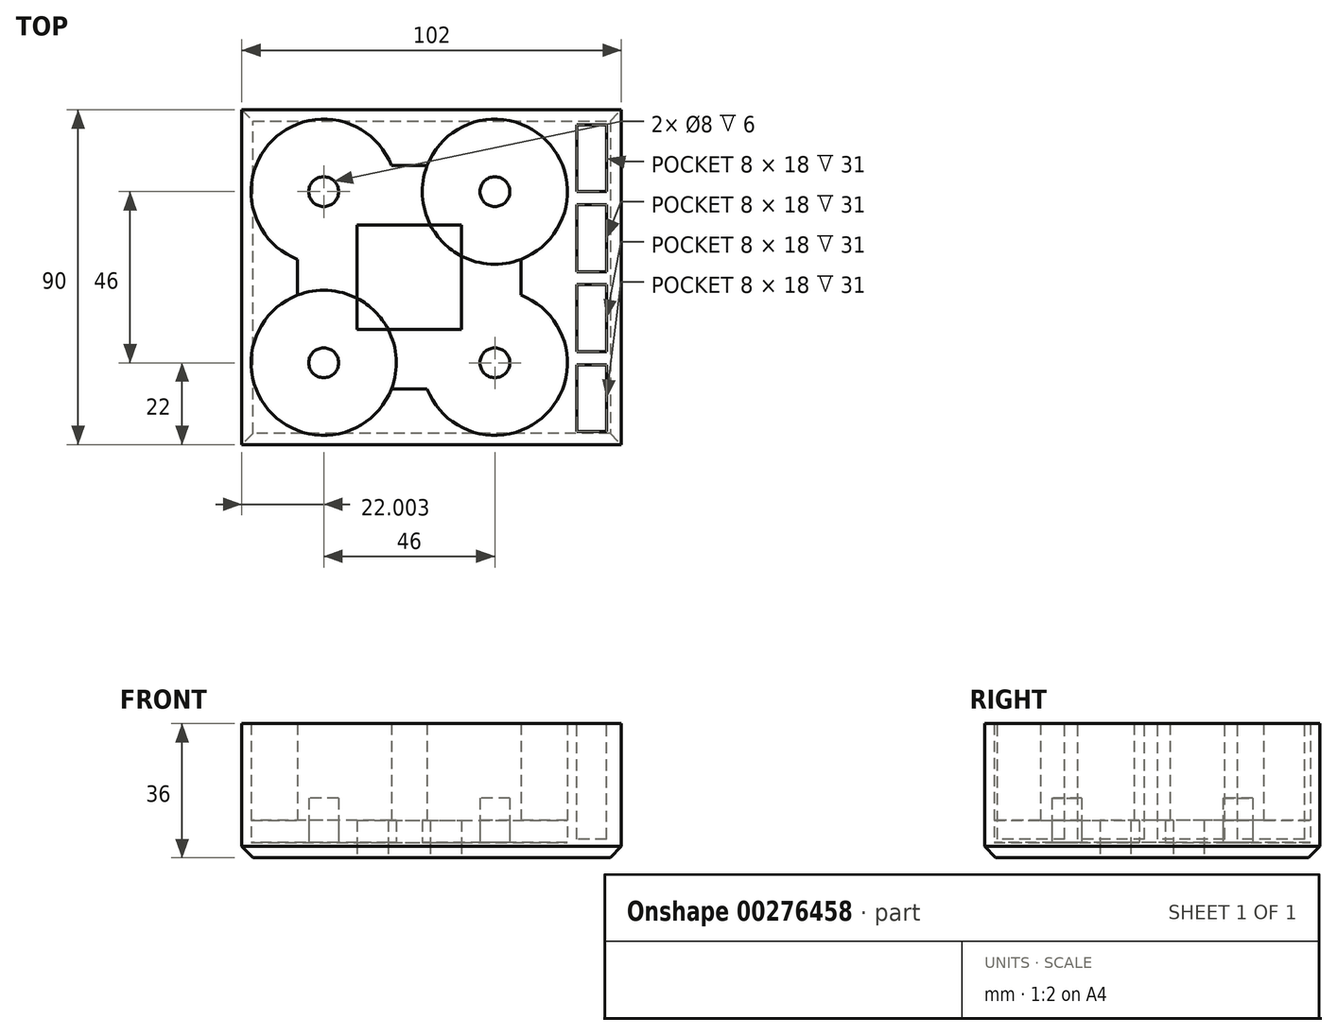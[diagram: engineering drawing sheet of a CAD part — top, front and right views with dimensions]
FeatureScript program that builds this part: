
annotation { "Feature Type Name" : "Feature", "Feature Type Description" : "" }
export const myFeature = defineFeature(function(context is Context, id is Id, definition is map)
    precondition{}
    {
        {
            var Q0;
            Q0=qCreatedBy(makeId("Top.planeOp"),FACE);
            var sketch = newSketch(context, id + "F0", { "sketchPlane" : qUnion([Q0])});
            skLineSegment(sketch, "E0.bottom", {"start": v(-22.74, 29.48) * mm, "end": v(31.26, 29.48) * mm, "construction": true});
            skLineSegment(sketch, "E0.top", {"start": v(-22.74, -24.52) * mm, "end": v(31.26, -24.52) * mm, "construction": true});
            skLineSegment(sketch, "E0.left", {"start": v(-22.74, 29.48) * mm, "end": v(-22.74, -24.52) * mm, "construction": true});
            skLineSegment(sketch, "E0.right", {"start": v(31.26, 29.48) * mm, "end": v(31.26, -24.52) * mm, "construction": true});
            skCircle(sketch, "E1", {"center": v(-18.74, 25.48) * mm, "radius": 4 * mm});
            skLineSegment(sketch, "E2", {"start": v(4.26, 29.48) * mm, "end": v(4.26, -24.52) * mm, "construction": true});
            skLineSegment(sketch, "E3", {"start": v(-22.74, 2.48) * mm, "end": v(31.26, 2.48) * mm, "construction": true});
            skCircle(sketch, "E4.MirrorC", {"center": v(27.26, 25.48) * mm, "radius": 4 * mm});
            skCircle(sketch, "E5.MirrorC", {"center": v(-18.74, -20.52) * mm, "radius": 4 * mm});
            skCircle(sketch, "E6.MirrorC", {"center": v(27.26, -20.52) * mm, "radius": 4 * mm});
            skCircle(sketch, "E7", {"center": v(-18.74, 25.48) * mm, "radius": 19.5 * mm});
            skCircle(sketch, "E8.MirrorC", {"center": v(27.26, 25.48) * mm, "radius": 19.5 * mm});
            skCircle(sketch, "E9.MirrorC", {"center": v(-18.74, -20.52) * mm, "radius": 19.5 * mm});
            skCircle(sketch, "E10.MirrorC", {"center": v(27.26, -20.52) * mm, "radius": 19.5 * mm});
            skLineSegment(sketch, "E11.bottom", {"start": v(-9.74, 16.48) * mm, "end": v(18.26, 16.48) * mm});
            skLineSegment(sketch, "E11.top", {"start": v(-9.74, -11.52) * mm, "end": v(18.26, -11.52) * mm});
            skLineSegment(sketch, "E11.left", {"start": v(-9.74, 16.48) * mm, "end": v(-9.74, -11.52) * mm});
            skLineSegment(sketch, "E11.right", {"start": v(18.26, 16.48) * mm, "end": v(18.26, -11.52) * mm});
            skLineSegment(sketch, "E12", {"start": v(-0.54, 32.48) * mm, "end": v(9.06, 32.48) * mm});
            skLineSegment(sketch, "E13.MirrorCS", {"start": v(-0.54, -27.52) * mm, "end": v(9.06, -27.52) * mm});
            skLineSegment(sketch, "E14", {"start": v(34.26, 7.28) * mm, "end": v(34.26, -2.32) * mm});
            skLineSegment(sketch, "E15.MirrorCS", {"start": v(-25.74, 7.28) * mm, "end": v(-25.74, -2.32) * mm});
            skLineSegment(sketch, "E16.bottom", {"start": v(-40.74, 47.48) * mm, "end": v(49.26, 47.48) * mm});
            skLineSegment(sketch, "E16.top", {"start": v(-40.74, -42.52) * mm, "end": v(49.26, -42.52) * mm});
            skLineSegment(sketch, "E16.left", {"start": v(-40.74, 47.48) * mm, "end": v(-40.74, -42.52) * mm});
            skLineSegment(sketch, "E16.right", {"start": v(49.26, 47.48) * mm, "end": v(49.26, -42.52) * mm});
            skSolve(sketch);
        }
        {
            var Q0;
            {var subQ3=sQuery(id+"F0.wireOp",EDGE,"E12");Q0=makeQuery(id+"F0.imprint","IMPRINT",FACE,{"disambiguationData":[TD([[makeQuery(id+"F0.imprint","IMPRINT",EDGE,{"derivedFrom":subQ3}),1.0]])]});}
            extrude(context, id + "F1", {"entities" : qUnion([Q0]), "depth" : 36 * mm});
        }
        {
            var Q0;
            Q0=makeQuery(id+"F0.imprint","IMPRINT",FACE,{"disambiguationData":[TD([[makeQuery(id+"F0.imprint","IMPRINT",EDGE,{"derivedFrom":sQuery(id+"F0.wireOp",EDGE,"E1")}),-1.0]])]});
            var Q1;
            Q1=makeQuery(id+"F0.imprint","IMPRINT",FACE,{"disambiguationData":[TD([[makeQuery(id+"F0.imprint","IMPRINT",EDGE,{"derivedFrom":sQuery(id+"F0.wireOp",EDGE,"E4.MirrorC")}),1.0]])]});
            var Q2;
            Q2=makeQuery(id+"F0.imprint","IMPRINT",FACE,{"disambiguationData":[TD([[makeQuery(id+"F0.imprint","IMPRINT",EDGE,{"derivedFrom":sQuery(id+"F0.wireOp",EDGE,"E6.MirrorC")}),-1.0]])]});
            var Q3;
            Q3=makeQuery(id+"F0.imprint","IMPRINT",FACE,{"disambiguationData":[TD([[makeQuery(id+"F0.imprint","IMPRINT",EDGE,{"derivedFrom":sQuery(id+"F0.wireOp",EDGE,"E5.MirrorC")}),1.0]])]});
            var Q4;
            {var subQ0=sQuery(id+"F0.wireOp",EDGE,"E12");Q4=makeQuery(id+"F0.imprint","IMPRINT",FACE,{"disambiguationData":[TD([[makeQuery(id+"F0.imprint","IMPRINT",EDGE,{"derivedFrom":subQ0}),-1.0]])]});}
            var Q5;
            {var subQ0=sQuery(id+"F0.wireOp",EDGE,"E15.MirrorCS");Q5=makeQuery(id+"F0.imprint","IMPRINT",FACE,{"disambiguationData":[TD([[makeQuery(id+"F0.imprint","IMPRINT",EDGE,{"derivedFrom":subQ0}),1.0]])]});}
            var Q6;
            {var subQ0=sQuery(id+"F0.wireOp",EDGE,"E14");Q6=makeQuery(id+"F0.imprint","IMPRINT",FACE,{"disambiguationData":[TD([[makeQuery(id+"F0.imprint","IMPRINT",EDGE,{"derivedFrom":subQ0}),-1.0]])]});}
            var Q7;
            {var subQ0=sQuery(id+"F0.wireOp",EDGE,"E13.MirrorCS");Q7=makeQuery(id+"F0.imprint","IMPRINT",FACE,{"disambiguationData":[TD([[makeQuery(id+"F0.imprint","IMPRINT",EDGE,{"derivedFrom":subQ0}),1.0]])]});}
            extrude(context, id + "F2", {"entities" : qUnion([Q0, Q1, Q2, Q3, Q4, Q5, Q6, Q7]), "operationType" : NewBodyOperationType.ADD, "depth" : 16 * mm});
        }
        {
            var Q0;
            Q0=makeQuery(id+"F0.imprint","IMPRINT",FACE,{"disambiguationData":[TD([[makeQuery(id+"F0.imprint","IMPRINT",EDGE,{"derivedFrom":sQuery(id+"F0.wireOp",EDGE,"E1")}),1.0]])]});
            var Q1;
            {var subQ5=sQuery(id+"F0.wireOp",EDGE,"E11.left");var subQ13=sQuery(id+"F0.wireOp",EDGE,"E7");var subQ14=makeQuery(id+"F0.imprint","INTERSECT",VERTEX,{"derivedFrom":[subQ13,subQ5]});Q1=makeQuery(id+"F0.imprint","IMPRINT",FACE,{"disambiguationData":[TD([[makeQuery(id+"F0.imprint","IMPRINT",EDGE,{"disambiguationData":[TD([[subQ14,-1.0]])],"derivedFrom":subQ13}),-1.0]])]});}
            var Q2;
            Q2=makeQuery(id+"F0.imprint","IMPRINT",FACE,{"disambiguationData":[TD([[makeQuery(id+"F0.imprint","IMPRINT",EDGE,{"derivedFrom":sQuery(id+"F0.wireOp",EDGE,"E4.MirrorC")}),-1.0]])]});
            var Q3;
            Q3=makeQuery(id+"F0.imprint","IMPRINT",FACE,{"disambiguationData":[TD([[makeQuery(id+"F0.imprint","IMPRINT",EDGE,{"derivedFrom":sQuery(id+"F0.wireOp",EDGE,"E6.MirrorC")}),1.0]])]});
            var Q4;
            {var subQ0=sQuery(id+"F0.wireOp",EDGE,"E11.right");var subQ1=sQuery(id+"F0.wireOp",EDGE,"E10.MirrorC");var subQ2=makeQuery(id+"F0.imprint","INTERSECT",VERTEX,{"derivedFrom":[subQ1,subQ0]});Q4=makeQuery(id+"F0.imprint","IMPRINT",FACE,{"disambiguationData":[TD([[makeQuery(id+"F0.imprint","IMPRINT",EDGE,{"disambiguationData":[TD([[subQ2,-1.0]])],"derivedFrom":subQ1}),1.0]])]});}
            var Q5;
            {var subQ0=sQuery(id+"F0.wireOp",EDGE,"E14");Q5=makeQuery(id+"F0.imprint","IMPRINT",FACE,{"disambiguationData":[TD([[makeQuery(id+"F0.imprint","IMPRINT",EDGE,{"derivedFrom":subQ0}),-1.0]])]});}
            var Q6;
            {var subQ0=sQuery(id+"F0.wireOp",EDGE,"E11.right");var subQ1=sQuery(id+"F0.wireOp",EDGE,"E8.MirrorC");var subQ2=makeQuery(id+"F0.imprint","INTERSECT",VERTEX,{"derivedFrom":[subQ1,subQ0]});Q6=makeQuery(id+"F0.imprint","IMPRINT",FACE,{"disambiguationData":[TD([[makeQuery(id+"F0.imprint","IMPRINT",EDGE,{"disambiguationData":[TD([[subQ2,-1.0]])],"derivedFrom":subQ1}),-1.0]])]});}
            var Q7;
            {var subQ0=sQuery(id+"F0.wireOp",EDGE,"E12");Q7=makeQuery(id+"F0.imprint","IMPRINT",FACE,{"disambiguationData":[TD([[makeQuery(id+"F0.imprint","IMPRINT",EDGE,{"derivedFrom":subQ0}),-1.0]])]});}
            var Q8;
            {var subQ0=sQuery(id+"F0.wireOp",EDGE,"E15.MirrorCS");Q8=makeQuery(id+"F0.imprint","IMPRINT",FACE,{"disambiguationData":[TD([[makeQuery(id+"F0.imprint","IMPRINT",EDGE,{"derivedFrom":subQ0}),1.0]])]});}
            var Q9;
            {var subQ0=sQuery(id+"F0.wireOp",EDGE,"E11.left");var subQ1=sQuery(id+"F0.wireOp",EDGE,"E7");var subQ2=makeQuery(id+"F0.imprint","INTERSECT",VERTEX,{"derivedFrom":[subQ1,subQ0]});Q9=makeQuery(id+"F0.imprint","IMPRINT",FACE,{"disambiguationData":[TD([[makeQuery(id+"F0.imprint","IMPRINT",EDGE,{"disambiguationData":[TD([[subQ2,-1.0]])],"derivedFrom":subQ1}),1.0]])]});}
            var Q10;
            {var subQ0=sQuery(id+"F0.wireOp",EDGE,"E13.MirrorCS");Q10=makeQuery(id+"F0.imprint","IMPRINT",FACE,{"disambiguationData":[TD([[makeQuery(id+"F0.imprint","IMPRINT",EDGE,{"derivedFrom":subQ0}),1.0]])]});}
            var Q11;
            {var subQ0=sQuery(id+"F0.wireOp",EDGE,"E11.left");var subQ1=sQuery(id+"F0.wireOp",EDGE,"E9.MirrorC");var subQ2=makeQuery(id+"F0.imprint","INTERSECT",VERTEX,{"derivedFrom":[subQ1,subQ0]});Q11=makeQuery(id+"F0.imprint","IMPRINT",FACE,{"disambiguationData":[TD([[makeQuery(id+"F0.imprint","IMPRINT",EDGE,{"disambiguationData":[TD([[subQ2,-1.0]])],"derivedFrom":subQ1}),-1.0]])]});}
            var Q12;
            Q12=makeQuery(id+"F0.imprint","IMPRINT",FACE,{"disambiguationData":[TD([[makeQuery(id+"F0.imprint","IMPRINT",EDGE,{"derivedFrom":sQuery(id+"F0.wireOp",EDGE,"E5.MirrorC")}),-1.0]])]});
            extrude(context, id + "F3", {"entities" : qUnion([Q0, Q1, Q2, Q3, Q4, Q5, Q6, Q7, Q8, Q9, Q10, Q11, Q12]), "operationType" : NewBodyOperationType.ADD, "depth" : 4 * mm});
        }
        {
            var Q0;
            Q0=makeQuery(id+"F1.opExtrude","CAP_FACE",FACE,{"disambiguationData":[OSD([sQuery(id+"F0.wireOp",EDGE,"E7"),sQuery(id+"F0.wireOp",EDGE,"E8.MirrorC"),sQuery(id+"F0.wireOp",EDGE,"E9.MirrorC"),sQuery(id+"F0.wireOp",EDGE,"E10.MirrorC"),sQuery(id+"F0.wireOp",EDGE,"E12"),sQuery(id+"F0.wireOp",EDGE,"E13.MirrorCS"),sQuery(id+"F0.wireOp",EDGE,"E14"),sQuery(id+"F0.wireOp",EDGE,"E15.MirrorCS"),sQuery(id+"F0.wireOp",EDGE,"E16.bottom"),sQuery(id+"F0.wireOp",EDGE,"E16.top"),sQuery(id+"F0.wireOp",EDGE,"E16.left"),sQuery(id+"F0.wireOp",EDGE,"E16.right")])],"isStart":false});
            var sketch = newSketch(context, id + "F4", { "sketchPlane" : qUnion([Q0])});
            skLineSegment(sketch, "E17.bottom", {"start": v(49.26, 43.48) * mm, "end": v(57.26, 43.48) * mm});
            skLineSegment(sketch, "E17.top", {"start": v(49.26, 25.48) * mm, "end": v(57.26, 25.48) * mm});
            skLineSegment(sketch, "E17.left", {"start": v(49.26, 43.48) * mm, "end": v(49.26, 25.48) * mm});
            skLineSegment(sketch, "E17.right", {"start": v(57.26, 43.48) * mm, "end": v(57.26, 25.48) * mm});
            skLineSegment(sketch, "E18.0.1.0", {"start": v(49.26, 3.98) * mm, "end": v(57.26, 3.98) * mm});
            skLineSegment(sketch, "E18.0.1.1", {"start": v(57.26, 21.98) * mm, "end": v(57.26, 3.98) * mm});
            skLineSegment(sketch, "E18.0.1.2", {"start": v(49.26, 21.98) * mm, "end": v(57.26, 21.98) * mm});
            skLineSegment(sketch, "E18.0.1.3", {"start": v(49.26, 21.98) * mm, "end": v(49.26, 3.98) * mm});
            skLineSegment(sketch, "E18.0.2.0", {"start": v(49.26, -17.52) * mm, "end": v(57.26, -17.52) * mm});
            skLineSegment(sketch, "E18.0.2.1", {"start": v(57.26, 0.48) * mm, "end": v(57.26, -17.52) * mm});
            skLineSegment(sketch, "E18.0.2.2", {"start": v(49.26, 0.48) * mm, "end": v(57.26, 0.48) * mm});
            skLineSegment(sketch, "E18.0.2.3", {"start": v(49.26, 0.48) * mm, "end": v(49.26, -17.52) * mm});
            skLineSegment(sketch, "E18.0.3.0", {"start": v(49.26, -39.02) * mm, "end": v(57.26, -39.02) * mm});
            skLineSegment(sketch, "E18.0.3.1", {"start": v(57.26, -21.02) * mm, "end": v(57.26, -39.02) * mm});
            skLineSegment(sketch, "E18.0.3.2", {"start": v(49.26, -21.02) * mm, "end": v(57.26, -21.02) * mm});
            skLineSegment(sketch, "E18.0.3.3", {"start": v(49.26, -21.02) * mm, "end": v(49.26, -39.02) * mm});
            skLineSegment(sketch, "E18.direction1", {"start": v(49.26, 25.48) * mm, "end": v(74.26, 25.48) * mm, "construction": true});
            skLineSegment(sketch, "E18.direction2", {"start": v(49.26, 25.48) * mm, "end": v(49.26, 3.98) * mm, "construction": true});
            skLineSegment(sketch, "E19.bottom", {"start": v(49.26, 47.48) * mm, "end": v(61.26, 47.48) * mm});
            skLineSegment(sketch, "E19.top", {"start": v(49.26, -42.52) * mm, "end": v(61.26, -42.52) * mm});
            skLineSegment(sketch, "E19.left", {"start": v(49.26, 47.48) * mm, "end": v(49.26, -42.52) * mm});
            skLineSegment(sketch, "E19.right", {"start": v(61.26, 47.48) * mm, "end": v(61.26, -42.52) * mm});
            skSolve(sketch);
        }
        {
            var Q0;
            {var subQ5=sQuery(id+"F4.wireOp",EDGE,"E17.bottom");Q0=makeQuery(id+"F4.imprint","IMPRINT",FACE,{"disambiguationData":[TD([[makeQuery(id+"F4.imprint","IMPRINT",EDGE,{"derivedFrom":subQ5}),1.0]])]});}
            var Q1;
            {var subQ0=sQuery(id+"F0.wireOp",EDGE,"E15.MirrorCS");var subQ1=sQuery(id+"F0.wireOp",EDGE,"E14");var subQ2=sQuery(id+"F0.wireOp",EDGE,"E13.MirrorCS");var subQ3=sQuery(id+"F0.wireOp",EDGE,"E12");var subQ4=sQuery(id+"F0.wireOp",EDGE,"E11.right");var subQ5=sQuery(id+"F0.wireOp",EDGE,"E11.left");var subQ6=sQuery(id+"F0.wireOp",EDGE,"E11.top");var subQ7=sQuery(id+"F0.wireOp",EDGE,"E11.bottom");var subQ8=sQuery(id+"F0.wireOp",EDGE,"E10.MirrorC");var subQ9=sQuery(id+"F0.wireOp",EDGE,"E9.MirrorC");var subQ10=sQuery(id+"F0.wireOp",EDGE,"E8.MirrorC");var subQ11=sQuery(id+"F0.wireOp",EDGE,"E7");var subQ12=sQuery(id+"F0.wireOp",EDGE,"E6.MirrorC");var subQ13=sQuery(id+"F0.wireOp",EDGE,"E5.MirrorC");var subQ14=sQuery(id+"F0.wireOp",EDGE,"E4.MirrorC");var subQ15=sQuery(id+"F0.wireOp",EDGE,"E1");Q1=makeQuery(id+"F3.boolean.opBoolean","MERGE",FACE,{"derivedFrom":[makeQuery(id+"F2.boolean.opBoolean","MERGE",FACE,{"derivedFrom":[makeQuery(id+"F1.opExtrude","CAP_FACE",FACE,{"disambiguationData":[OSD([subQ11,subQ10,subQ9,subQ8,subQ3,subQ2,subQ1,subQ0,sQuery(id+"F0.wireOp",EDGE,"E16.bottom"),sQuery(id+"F0.wireOp",EDGE,"E16.top"),sQuery(id+"F0.wireOp",EDGE,"E16.left"),sQuery(id+"F0.wireOp",EDGE,"E16.right")])],"isStart":true}),makeQuery(id+"F2.opExtrude","CAP_FACE",FACE,{"disambiguationData":[OSD([subQ15,subQ14,subQ13,subQ12,subQ11,subQ10,subQ9,subQ8,subQ7,subQ6,subQ5,subQ4,subQ3,subQ2,subQ1,subQ0])],"isStart":true})]}),makeQuery(id+"F3.opExtrude","CAP_FACE",FACE,{"disambiguationData":[OSD([subQ15])],"isStart":true}),makeQuery(id+"F3.opExtrude","CAP_FACE",FACE,{"disambiguationData":[OSD([subQ14])],"isStart":true}),makeQuery(id+"F3.opExtrude","CAP_FACE",FACE,{"disambiguationData":[OSD([subQ13])],"isStart":true}),makeQuery(id+"F3.opExtrude","CAP_FACE",FACE,{"disambiguationData":[OSD([subQ12])],"isStart":true}),makeQuery(id+"F3.opExtrude","CAP_FACE",FACE,{"disambiguationData":[OSD([subQ11,subQ10,subQ9,subQ8,subQ7,subQ6,subQ5,subQ4,subQ3,subQ2,subQ1,subQ0])],"isStart":true})]});}
            extrude(context, id + "F5", {"entities" : qUnion([Q0]), "operationType" : NewBodyOperationType.ADD, "endBound" : BoundingType.UP_TO_SURFACE, "oppositeDirection" : true, "endBoundEntityFace" : qUnion([Q1]), "depth" : 25 * mm});
        }
        {
            var Q0;
            {var subQ0=sQuery(id+"F0.wireOp",EDGE,"E15.MirrorCS");var subQ1=sQuery(id+"F0.wireOp",EDGE,"E14");var subQ2=sQuery(id+"F0.wireOp",EDGE,"E13.MirrorCS");var subQ3=sQuery(id+"F0.wireOp",EDGE,"E12");var subQ4=sQuery(id+"F0.wireOp",EDGE,"E11.right");var subQ5=sQuery(id+"F0.wireOp",EDGE,"E11.left");var subQ6=sQuery(id+"F0.wireOp",EDGE,"E11.top");var subQ7=sQuery(id+"F0.wireOp",EDGE,"E11.bottom");var subQ8=sQuery(id+"F0.wireOp",EDGE,"E10.MirrorC");var subQ9=sQuery(id+"F0.wireOp",EDGE,"E9.MirrorC");var subQ10=sQuery(id+"F0.wireOp",EDGE,"E8.MirrorC");var subQ11=sQuery(id+"F0.wireOp",EDGE,"E7");var subQ12=sQuery(id+"F0.wireOp",EDGE,"E6.MirrorC");var subQ13=sQuery(id+"F0.wireOp",EDGE,"E5.MirrorC");var subQ14=sQuery(id+"F0.wireOp",EDGE,"E4.MirrorC");var subQ15=sQuery(id+"F0.wireOp",EDGE,"E1");Q0=makeQuery(id+"F5.boolean.opBoolean","MERGE",FACE,{"derivedFrom":[makeQuery(id+"F3.boolean.opBoolean","MERGE",FACE,{"derivedFrom":[makeQuery(id+"F2.boolean.opBoolean","MERGE",FACE,{"derivedFrom":[makeQuery(id+"F1.opExtrude","CAP_FACE",FACE,{"disambiguationData":[OSD([subQ11,subQ10,subQ9,subQ8,subQ3,subQ2,subQ1,subQ0,sQuery(id+"F0.wireOp",EDGE,"E16.bottom"),sQuery(id+"F0.wireOp",EDGE,"E16.top"),sQuery(id+"F0.wireOp",EDGE,"E16.left"),sQuery(id+"F0.wireOp",EDGE,"E16.right")])],"isStart":true}),makeQuery(id+"F2.opExtrude","CAP_FACE",FACE,{"disambiguationData":[OSD([subQ15,subQ14,subQ13,subQ12,subQ11,subQ10,subQ9,subQ8,subQ7,subQ6,subQ5,subQ4,subQ3,subQ2,subQ1,subQ0])],"isStart":true})]}),makeQuery(id+"F3.opExtrude","CAP_FACE",FACE,{"disambiguationData":[OSD([subQ15])],"isStart":true}),makeQuery(id+"F3.opExtrude","CAP_FACE",FACE,{"disambiguationData":[OSD([subQ14])],"isStart":true}),makeQuery(id+"F3.opExtrude","CAP_FACE",FACE,{"disambiguationData":[OSD([subQ13])],"isStart":true}),makeQuery(id+"F3.opExtrude","CAP_FACE",FACE,{"disambiguationData":[OSD([subQ12])],"isStart":true}),makeQuery(id+"F3.opExtrude","CAP_FACE",FACE,{"disambiguationData":[OSD([subQ11,subQ10,subQ9,subQ8,subQ7,subQ6,subQ5,subQ4,subQ3,subQ2,subQ1,subQ0])],"isStart":true})]}),makeQuery(id+"F5.opExtrude","CAP_FACE",FACE,{"disambiguationData":[OSD([sQuery(id+"F4.wireOp",EDGE,"E17.bottom"),sQuery(id+"F4.wireOp",EDGE,"E17.top"),sQuery(id+"F4.wireOp",EDGE,"E17.right"),sQuery(id+"F4.wireOp",EDGE,"E18.0.1.0"),sQuery(id+"F4.wireOp",EDGE,"E18.0.1.1"),sQuery(id+"F4.wireOp",EDGE,"E18.0.1.2"),sQuery(id+"F4.wireOp",EDGE,"E18.0.2.0"),sQuery(id+"F4.wireOp",EDGE,"E18.0.2.1"),sQuery(id+"F4.wireOp",EDGE,"E18.0.2.2"),sQuery(id+"F4.wireOp",EDGE,"E18.0.3.0"),sQuery(id+"F4.wireOp",EDGE,"E18.0.3.1"),sQuery(id+"F4.wireOp",EDGE,"E18.0.3.2"),sQuery(id+"F4.wireOp",EDGE,"E19.bottom"),sQuery(id+"F4.wireOp",EDGE,"E19.top"),sQuery(id+"F4.wireOp",EDGE,"E19.left"),sQuery(id+"F4.wireOp",EDGE,"E19.right")])],"isStart":false})]});}
            var sketch = newSketch(context, id + "F6", { "sketchPlane" : qUnion([Q0])});
            skLineSegment(sketch, "E20.0", {"start": v(49.26, -43.48) * mm, "end": v(49.26, -25.48) * mm});
            skLineSegment(sketch, "E20.1", {"start": v(57.26, -25.48) * mm, "end": v(57.26, -43.48) * mm});
            skLineSegment(sketch, "E20.2", {"start": v(57.26, -25.48) * mm, "end": v(49.26, -25.48) * mm});
            skLineSegment(sketch, "E20.3", {"start": v(57.26, -43.48) * mm, "end": v(49.26, -43.48) * mm});
            skLineSegment(sketch, "E20.4", {"start": v(49.26, -21.98) * mm, "end": v(49.26, -3.98) * mm});
            skLineSegment(sketch, "E20.5", {"start": v(57.26, -21.98) * mm, "end": v(49.26, -21.98) * mm});
            skLineSegment(sketch, "E20.6", {"start": v(57.26, -3.98) * mm, "end": v(57.26, -21.98) * mm});
            skLineSegment(sketch, "E21.0", {"start": v(57.26, -3.98) * mm, "end": v(49.26, -3.98) * mm});
            skLineSegment(sketch, "E22.0", {"start": v(57.26, -0.48) * mm, "end": v(49.26, -0.48) * mm});
            skLineSegment(sketch, "E22.1", {"start": v(49.26, -0.48) * mm, "end": v(49.26, 17.52) * mm});
            skLineSegment(sketch, "E22.2", {"start": v(57.26, 17.52) * mm, "end": v(57.26, -0.48) * mm});
            skLineSegment(sketch, "E22.3", {"start": v(57.26, 17.52) * mm, "end": v(49.26, 17.52) * mm});
            skLineSegment(sketch, "E23.0", {"start": v(57.26, 39.02) * mm, "end": v(57.26, 21.02) * mm});
            skLineSegment(sketch, "E23.1", {"start": v(49.26, 21.02) * mm, "end": v(49.26, 39.02) * mm});
            skLineSegment(sketch, "E23.2", {"start": v(57.26, 21.02) * mm, "end": v(49.26, 21.02) * mm});
            skLineSegment(sketch, "E23.3", {"start": v(57.26, 39.02) * mm, "end": v(49.26, 39.02) * mm});
            skSolve(sketch);
        }
        {
            var Q0;
            Q0=makeQuery(id+"F6.imprint","IMPRINT",FACE,{"disambiguationData":[TD([[makeQuery(id+"F6.imprint","IMPRINT",EDGE,{"derivedFrom":sQuery(id+"F6.wireOp",EDGE,"E23.0")}),-1.0]])]});
            var Q1;
            Q1=makeQuery(id+"F6.imprint","IMPRINT",FACE,{"disambiguationData":[TD([[makeQuery(id+"F6.imprint","IMPRINT",EDGE,{"derivedFrom":sQuery(id+"F6.wireOp",EDGE,"E22.0")}),-1.0]])]});
            var Q2;
            Q2=makeQuery(id+"F6.imprint","IMPRINT",FACE,{"disambiguationData":[TD([[makeQuery(id+"F6.imprint","IMPRINT",EDGE,{"derivedFrom":sQuery(id+"F6.wireOp",EDGE,"E20.4")}),-1.0]])]});
            var Q3;
            Q3=makeQuery(id+"F6.imprint","IMPRINT",FACE,{"disambiguationData":[TD([[makeQuery(id+"F6.imprint","IMPRINT",EDGE,{"derivedFrom":sQuery(id+"F6.wireOp",EDGE,"E20.0")}),-1.0]])]});
            extrude(context, id + "F7", {"entities" : qUnion([Q0, Q1, Q2, Q3]), "operationType" : NewBodyOperationType.ADD, "oppositeDirection" : true, "depth" : 5 * mm});
        }
        {
            var Q0;
            Q0=makeQuery(id+"F2.opExtrude","CAP_FACE",FACE,{"disambiguationData":[OSD([sQuery(id+"F0.wireOp",EDGE,"E1"),sQuery(id+"F0.wireOp",EDGE,"E4.MirrorC"),sQuery(id+"F0.wireOp",EDGE,"E5.MirrorC"),sQuery(id+"F0.wireOp",EDGE,"E6.MirrorC"),sQuery(id+"F0.wireOp",EDGE,"E7"),sQuery(id+"F0.wireOp",EDGE,"E8.MirrorC"),sQuery(id+"F0.wireOp",EDGE,"E9.MirrorC"),sQuery(id+"F0.wireOp",EDGE,"E10.MirrorC"),sQuery(id+"F0.wireOp",EDGE,"E11.bottom"),sQuery(id+"F0.wireOp",EDGE,"E11.top"),sQuery(id+"F0.wireOp",EDGE,"E11.left"),sQuery(id+"F0.wireOp",EDGE,"E11.right"),sQuery(id+"F0.wireOp",EDGE,"E12"),sQuery(id+"F0.wireOp",EDGE,"E13.MirrorCS"),sQuery(id+"F0.wireOp",EDGE,"E14"),sQuery(id+"F0.wireOp",EDGE,"E15.MirrorCS")])],"isStart":false});
            extrude(context, id + "F8", {"entities" : qUnion([Q0]), "operationType" : NewBodyOperationType.REMOVE, "oppositeDirection" : true, "depth" : 6 * mm});
        }
        {
            var Q0;
            Q0=makeQuery(id+"F5.boolean.opBoolean","MERGE",EDGE,{"derivedFrom":[makeQuery(id+"F1.opExtrude","CAP_EDGE",EDGE,{"disambiguationData":[OSD([sQuery(id+"F0.wireOp",EDGE,"E16.bottom")])],"isStart":true}),makeQuery(id+"F5.opExtrude","CAP_EDGE",EDGE,{"disambiguationData":[OSD([sQuery(id+"F4.wireOp",EDGE,"E19.bottom")])],"isStart":false})]});
            var Q1;
            Q1=makeQuery(id+"F5.opExtrude","CAP_EDGE",EDGE,{"disambiguationData":[OSD([sQuery(id+"F4.wireOp",EDGE,"E19.right")])],"isStart":false});
            var Q2;
            Q2=makeQuery(id+"F5.boolean.opBoolean","MERGE",EDGE,{"derivedFrom":[makeQuery(id+"F1.opExtrude","CAP_EDGE",EDGE,{"disambiguationData":[OSD([sQuery(id+"F0.wireOp",EDGE,"E16.top")])],"isStart":true}),makeQuery(id+"F5.opExtrude","CAP_EDGE",EDGE,{"disambiguationData":[OSD([sQuery(id+"F4.wireOp",EDGE,"E19.top")])],"isStart":false})]});
            var Q3;
            Q3=makeQuery(id+"F1.opExtrude","CAP_EDGE",EDGE,{"disambiguationData":[OSD([sQuery(id+"F0.wireOp",EDGE,"E16.left")])],"isStart":true});
            chamfer(context, id + "F9", {"entities" : qUnion([Q0, Q1, Q2, Q3]), "width" : 3 * mm, "tangentPropagation" : true});
        }
    });
